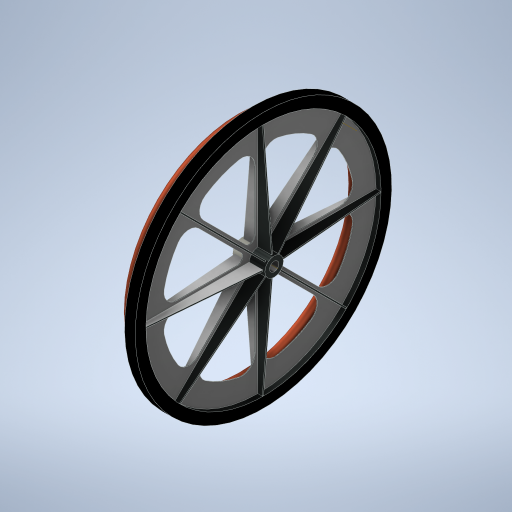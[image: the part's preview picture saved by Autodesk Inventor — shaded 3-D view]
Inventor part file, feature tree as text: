
AUTODESK INVENTOR PART (.ipt)
format: ipt  version: 2023 (Build 270158000, 158)  size: 548,864 bytes
history: native  units: in
note: dims shown in document units (in); Inventor stores cm internally (conversion verified against a paired STEP export)
features: sketch x10, extrude x6, other x4, plane x2, loft x1, pattern_circular x1, revolve x1
ambient origin geometry x8: Origin, YZ Plane, XZ Plane, XY Plane, X Axis, Y Axis, Z Axis, Center Point
bodies: Solid1 (feature_tree)
feature tree (25):
  extrude  "Extrusion1"  Depth=1.5in TaperAngle=0.0deg
  extrude  "Extrusion2"  Depth=0.03in TaperAngle=0.0deg
  extrude  "Extrusion3"  Depth=0.5in TaperAngle=0.0deg
  extrude  "Extrusion4"  Depth=2.0in
  plane  "Work Plane1"
  loft  "Loft1"
  other  "Work Axis1"
  extrude  "Extrusion5"  Depth=1.25in
  pattern_circular  "Circular Pattern1"  [2 undecoded]
  extrude  "Extrusion6"  Depth=0.125in
  plane  "Work Plane2"
  other  "Work Axis2"
  sketch  "Sketch9"  dims[d24=0.125in]
  other  "Work Axis3"
  sketch  "Sketch10"  dims[d25=0.125in d26=0.875in d27=0.125in d28=0.0in d29=90.0deg d30=0.0in d31=90.0deg d32=0.4375in d33=10.5in d34=1.125in d35=0.0in d36=3.1496in d37=360.0deg d39=0.875in d40=14.0625in d41=0.0in d42=0.75in d43=90.0deg]
  revolve  "Revolution1"  Angle=90.0deg
  sketch  "Sketch1"  dims[d0=1.75in d1=1.5in d2=1.5in d3=0.0in d4=0.0in]
  sketch  "Sketch2"  dims[d5=24.0in d6=0.03in d7=0.03in d8=0.0in d9=0.0in]
  sketch  "Sketch3"  dims[d10=1.0in d11=0.5in d12=0.5in d13=0.0in d14=0.0in]
  sketch  "Sketch4"  dims[d15=45.0deg d16=2.0in]
  sketch  "Sketch5"  dims[d17=0.625in d18=0.625in]
  sketch  "Sketch6"  dims[d19=0.5in d20=1.25in]
  sketch  "Sketch7"  dims[d21=6.5in d22=0.0in]
  sketch  "Sketch8"  dims[d23=11.1in]
  other  "Work Point1"
note: 2 required parameter values undecoded (feature->parameter linkage not recoverable at this tier; creation-order binding heuristic only, values carry confidence <= 0.55)
